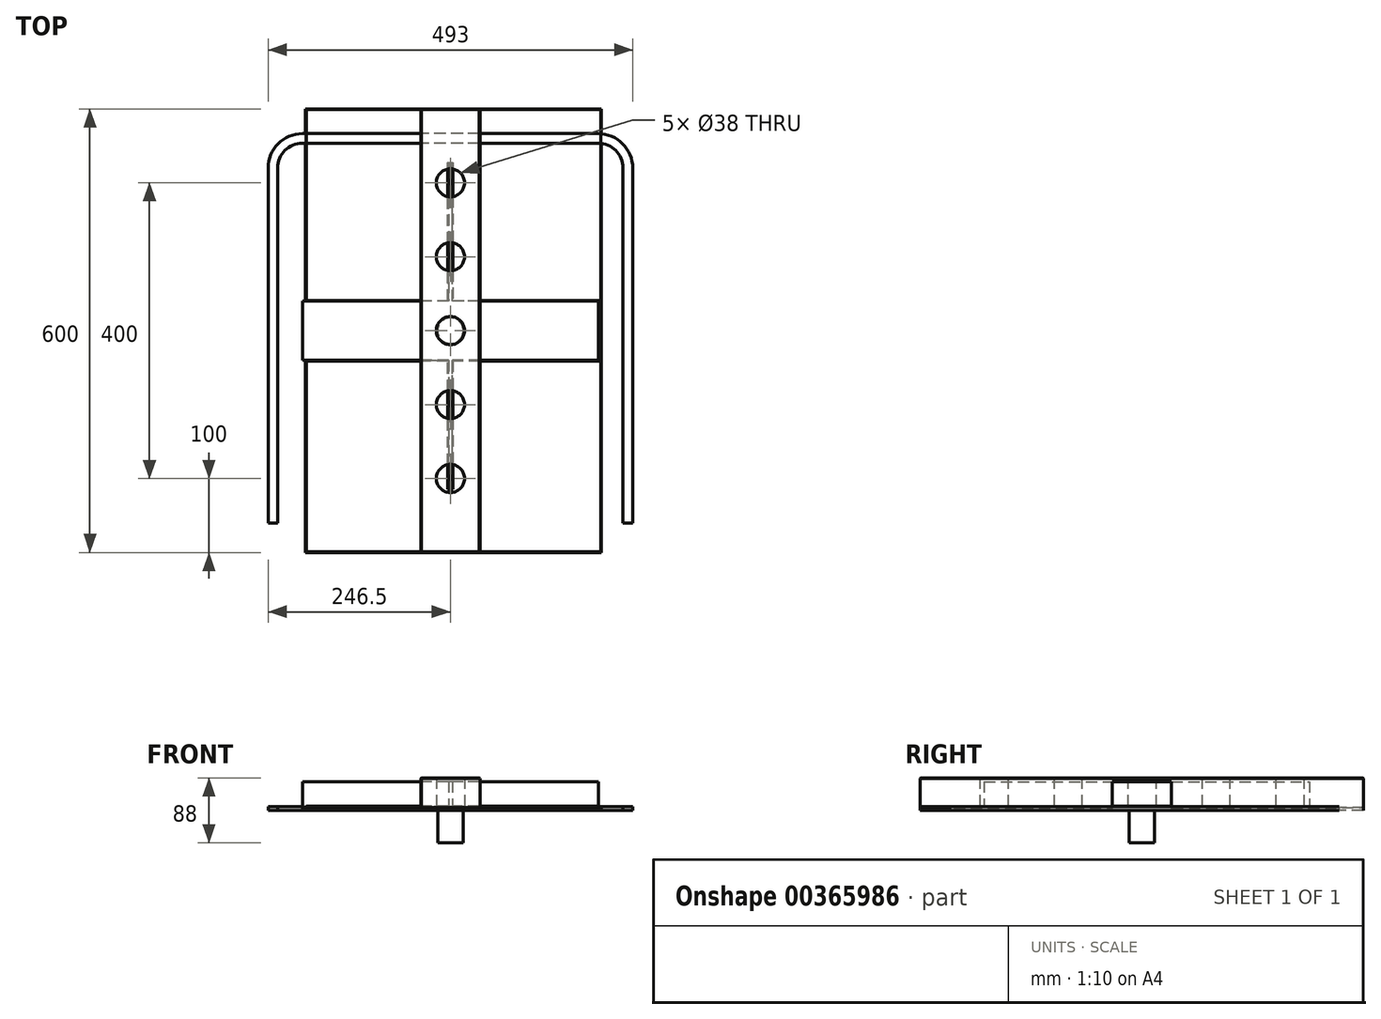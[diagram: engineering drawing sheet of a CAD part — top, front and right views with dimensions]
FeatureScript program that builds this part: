
annotation { "Feature Type Name" : "Feature", "Feature Type Description" : "" }
export const myFeature = defineFeature(function(context is Context, id is Id, definition is map)
    precondition{}
    {
        {
            var Q0;
            Q0=qCreatedBy(makeId("Top.planeOp"),FACE);
            var sketch = newSketch(context, id + "F0", { "sketchPlane" : qUnion([Q0])});
            skLineSegment(sketch, "E0.bottom", {"start": v(40, 300) * mm, "end": v(-40, 300) * mm});
            skLineSegment(sketch, "E0.top", {"start": v(40, -300) * mm, "end": v(-40, -300) * mm});
            skLineSegment(sketch, "E0.left", {"start": v(40, 300) * mm, "end": v(40, -300) * mm});
            skLineSegment(sketch, "E0.right", {"start": v(-40, 300) * mm, "end": v(-40, -300) * mm});
            skCircle(sketch, "E1", {"center": v(0, 200) * mm, "radius": 19 * mm});
            skCircle(sketch, "E2", {"center": v(0, 100) * mm, "radius": 19 * mm});
            skCircle(sketch, "E3", {"center": v(0, 0) * mm, "radius": 19 * mm});
            skCircle(sketch, "E4", {"center": v(0, -100) * mm, "radius": 19 * mm});
            skCircle(sketch, "E5", {"center": v(0, -200) * mm, "radius": 19 * mm});
            skSolve(sketch);
        }
        {
            var Q0;
            Q0=makeQuery(id+"F0.imprint","IMPRINT",FACE,{"disambiguationData":[TD([[makeQuery(id+"F0.imprint","IMPRINT",EDGE,{"derivedFrom":sQuery(id+"F0.wireOp",EDGE,"E0.bottom")}),1.0]])]});
            extrude(context, id + "F1", {"entities" : qUnion([Q0]), "depth" : 44 * mm});
        }
        {
            var Q0;
            Q0=qCreatedBy(makeId("Top.planeOp"),FACE);
            var sketch = newSketch(context, id + "F2", { "sketchPlane" : qUnion([Q0])});
            skLineSegment(sketch, "E6.bottom", {"start": v(200, 40) * mm, "end": v(-200, 40) * mm});
            skLineSegment(sketch, "E6.top", {"start": v(200, -40) * mm, "end": v(-200, -40) * mm});
            skLineSegment(sketch, "E6.left", {"start": v(200, 40) * mm, "end": v(200, -40) * mm});
            skLineSegment(sketch, "E6.right", {"start": v(-200, 40) * mm, "end": v(-200, -40) * mm});
            skPoint(sketch, "E6.middle", {"position": v(0, 0) * mm});
            skSolve(sketch);
        }
        {
            var Q0;
            Q0=makeQuery(id+"F2.imprint","IMPRINT",FACE,{"disambiguationData":[TD([[makeQuery(id+"F2.imprint","IMPRINT",EDGE,{"derivedFrom":sQuery(id+"F2.wireOp",EDGE,"E6.bottom")}),1.0]])]});
            extrude(context, id + "F3", {"entities" : qUnion([Q0]), "depth" : 39 * mm});
        }
        {
            var Q0;
            Q0=qCreatedBy(makeId("Top.planeOp"),FACE);
            var sketch = newSketch(context, id + "F4", { "sketchPlane" : qUnion([Q0])});
            skLineSegment(sketch, "E7.bottom", {"start": v(204.1, -300) * mm, "end": v(-195.9, -300) * mm});
            skLineSegment(sketch, "E7.top", {"start": v(204.1, 300) * mm, "end": v(-195.9, 300) * mm});
            skLineSegment(sketch, "E7.left", {"start": v(204.1, -300) * mm, "end": v(204.1, 300) * mm});
            skLineSegment(sketch, "E7.right", {"start": v(-195.9, -300) * mm, "end": v(-195.9, 300) * mm});
            skPoint(sketch, "E7.middle", {"position": v(4.1, 0) * mm});
            skSolve(sketch);
        }
        {
            var Q0;
            Q0=makeQuery(id+"F4.imprint","IMPRINT",FACE,{"disambiguationData":[TD([[makeQuery(id+"F4.imprint","IMPRINT",EDGE,{"derivedFrom":sQuery(id+"F4.wireOp",EDGE,"E7.bottom")}),-1.0]])]});
            extrude(context, id + "F5", {"entities" : qUnion([Q0]), "depth" : 5 * mm});
        }
        {
            var Q0;
            Q0=qCreatedBy(makeId("Top.planeOp"),FACE);
            var sketch = newSketch(context, id + "F6", { "sketchPlane" : qUnion([Q0])});
            skLineSegment(sketch, "E8.bottom", {"start": v(2.5, -213.42) * mm, "end": v(-2.5, -213.42) * mm});
            skLineSegment(sketch, "E8.top", {"start": v(2.5, 226.58) * mm, "end": v(-2.5, 226.58) * mm});
            skLineSegment(sketch, "E8.left", {"start": v(2.5, -213.42) * mm, "end": v(2.5, 226.58) * mm});
            skLineSegment(sketch, "E8.right", {"start": v(-2.5, -213.42) * mm, "end": v(-2.5, 226.58) * mm});
            skPoint(sketch, "E8.middle", {"position": v(0, 6.58) * mm});
            skSolve(sketch);
        }
        {
            var Q0;
            Q0=makeQuery(id+"F6.imprint","IMPRINT",FACE,{"disambiguationData":[TD([[makeQuery(id+"F6.imprint","IMPRINT",EDGE,{"derivedFrom":sQuery(id+"F6.wireOp",EDGE,"E8.bottom")}),-1.0]])]});
            extrude(context, id + "F7", {"entities" : qUnion([Q0]), "depth" : 39 * mm});
        }
        {
            var Q0;
            Q0=qCreatedBy(makeId("Top.planeOp"),FACE);
            var sketch = newSketch(context, id + "F8", { "sketchPlane" : qUnion([Q0])});
            skCircle(sketch, "E9", {"center": v(0, 0) * mm, "radius": 17.25 * mm});
            skCircle(sketch, "E10", {"center": v(0, 0) * mm, "radius": 18.9 * mm});
            skSolve(sketch);
        }
        {
            var Q0;
            Q0=makeQuery(id+"F8.imprint","IMPRINT",FACE,{"disambiguationData":[TD([[makeQuery(id+"F8.imprint","IMPRINT",EDGE,{"derivedFrom":sQuery(id+"F8.wireOp",EDGE,"E9")}),1.0]])]});
            extrude(context, id + "F9", {"entities" : qUnion([Q0]), "depth" : -44 * mm});
        }
        {
            var Q0;
            Q0=makeQuery(id+"F8.imprint","IMPRINT",FACE,{"disambiguationData":[TD([[makeQuery(id+"F8.imprint","IMPRINT",EDGE,{"derivedFrom":sQuery(id+"F8.wireOp",EDGE,"E9")}),1.0]])]});
            var Q1;
            Q1=makeQuery(id+"F8.imprint","IMPRINT",FACE,{"disambiguationData":[TD([[makeQuery(id+"F8.imprint","IMPRINT",EDGE,{"derivedFrom":sQuery(id+"F8.wireOp",EDGE,"E9")}),-1.0]])]});
            extrude(context, id + "F10", {"entities" : qUnion([Q0, Q1]), "operationType" : NewBodyOperationType.ADD, "depth" : 11 * mm});
        }
        {
            var Q0;
            Q0=qCreatedBy(makeId("Top.planeOp"),FACE);
            var sketch = newSketch(context, id + "F11", { "sketchPlane" : qUnion([Q0])});
            skLineSegment(sketch, "E11.top", {"start": v(200, 260) * mm, "end": v(-200, 260) * mm});
            skLineSegment(sketch, "E11.left", {"start": v(240, -260) * mm, "end": v(240, 220) * mm});
            skLineSegment(sketch, "E11.right", {"start": v(-240, -260) * mm, "end": v(-240, 220) * mm});
            skPoint(sketch, "E11.middle", {"position": v(0, 0) * mm});
            skPoint(sketch, "E12", {"position": v(240, 0) * mm});
            skPoint(sketch, "E13.visualSharp", {"position": v(-240, 260) * mm});
            skArc(sketch, "E13.filletArc", {"start": v(-200, 260) * mm, "mid": v(-228.28, 248.28) * mm, "end": v(-240, 220) * mm});
            skPoint(sketch, "E14.visualSharp", {"position": v(240, 260) * mm});
            skArc(sketch, "E14.filletArc", {"start": v(240, 220) * mm, "mid": v(228.28, 248.28) * mm, "end": v(200, 260) * mm});
            skLineSegment(sketch, "E15.0", {"start": v(233.5, -260) * mm, "end": v(233.5, 220) * mm});
            skLineSegment(sketch, "E15.1", {"start": v(-233.5, -260) * mm, "end": v(-233.5, 220) * mm});
            skArc(sketch, "E15.2", {"start": v(-200, 253.5) * mm, "mid": v(-223.69, 243.69) * mm, "end": v(-233.5, 220) * mm});
            skLineSegment(sketch, "E15.3", {"start": v(200, 253.5) * mm, "end": v(-200, 253.5) * mm});
            skArc(sketch, "E15.4", {"start": v(233.5, 220) * mm, "mid": v(223.69, 243.69) * mm, "end": v(200, 253.5) * mm});
            skLineSegment(sketch, "E16.0", {"start": v(246.5, -260) * mm, "end": v(246.5, 220) * mm});
            skLineSegment(sketch, "E16.1", {"start": v(-246.5, -260) * mm, "end": v(-246.5, 220) * mm});
            skArc(sketch, "E16.2", {"start": v(-200, 266.5) * mm, "mid": v(-232.88, 252.88) * mm, "end": v(-246.5, 220) * mm});
            skLineSegment(sketch, "E16.3", {"start": v(200, 266.5) * mm, "end": v(-200, 266.5) * mm});
            skArc(sketch, "E16.4", {"start": v(246.5, 220) * mm, "mid": v(232.88, 252.88) * mm, "end": v(200, 266.5) * mm});
            skLineSegment(sketch, "E17", {"start": v(-246.5, -260) * mm, "end": v(-233.5, -260) * mm});
            skLineSegment(sketch, "E18", {"start": v(233.5, -260) * mm, "end": v(246.5, -260) * mm});
            skSolve(sketch);
        }
        {
            var Q0;
            Q0=makeQuery(id+"F11.imprint","IMPRINT",FACE,{"disambiguationData":[TD([[makeQuery(id+"F11.imprint","IMPRINT",EDGE,{"derivedFrom":sQuery(id+"F11.wireOp",EDGE,"E11.top")}),-1.0]])]});
            var Q1;
            Q1=makeQuery(id+"F11.imprint","IMPRINT",FACE,{"disambiguationData":[TD([[makeQuery(id+"F11.imprint","IMPRINT",EDGE,{"derivedFrom":sQuery(id+"F11.wireOp",EDGE,"E11.top")}),1.0]])]});
            extrude(context, id + "F12", {"entities" : qUnion([Q0, Q1]), "depth" : 5 * mm});
        }
        {
            var Q0;
            Q0=makeQuery(id+"F1.opExtrude","CAP_EDGE",EDGE,{"disambiguationData":[OSD([sQuery(id+"F0.wireOp",EDGE,"E0.left")])],"isStart":false});
            var Q1;
            Q1=makeQuery(id+"F1.opExtrude","CAP_EDGE",EDGE,{"disambiguationData":[OSD([sQuery(id+"F0.wireOp",EDGE,"E0.right")])],"isStart":false});
            var Q2;
            Q2=makeQuery(id+"F1.opExtrude","CAP_EDGE",EDGE,{"disambiguationData":[OSD([sQuery(id+"F0.wireOp",EDGE,"E0.top")])],"isStart":false});
            var Q3;
            Q3=makeQuery(id+"F1.opExtrude","CAP_EDGE",EDGE,{"disambiguationData":[OSD([sQuery(id+"F0.wireOp",EDGE,"E0.bottom")])],"isStart":false});
            var Q4;
            Q4=makeQuery(id+"F1.opExtrude","SWEPT_EDGE",EDGE,{"disambiguationData":[OSD([sQuery(id+"F0.wireOp",EDGE,"E0.top"),sQuery(id+"F0.wireOp",EDGE,"E0.right")])]});
            var Q5;
            Q5=makeQuery(id+"F1.opExtrude","SWEPT_EDGE",EDGE,{"disambiguationData":[OSD([sQuery(id+"F0.wireOp",EDGE,"E0.bottom"),sQuery(id+"F0.wireOp",EDGE,"E0.right")])]});
            chamfer(context, id + "F13", {"entities" : qUnion([Q0, Q1, Q2, Q3, Q4, Q5]), "width" : 1 * mm, "tangentPropagation" : true});
        }
        {
            var Q0;
            Q0=makeQuery(id+"F5.opExtrude","CAP_FACE",FACE,{"disambiguationData":[OSD([sQuery(id+"F4.wireOp",EDGE,"E7.bottom"),sQuery(id+"F4.wireOp",EDGE,"E7.top"),sQuery(id+"F4.wireOp",EDGE,"E7.left"),sQuery(id+"F4.wireOp",EDGE,"E7.right")])],"isStart":false});
            chamfer(context, id + "F14", {"entities" : qUnion([Q0]), "width" : 1 * mm, "tangentPropagation" : true});
        }
    });
